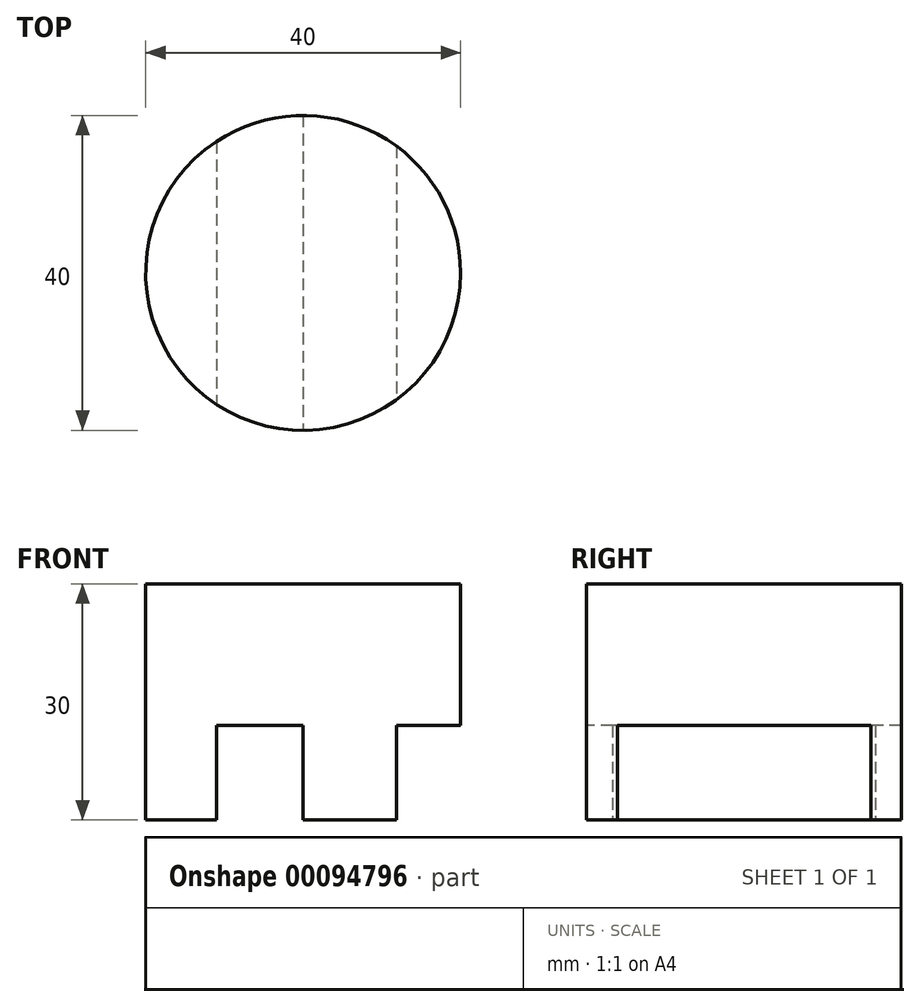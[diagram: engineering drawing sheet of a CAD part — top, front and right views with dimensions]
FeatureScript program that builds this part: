
annotation { "Feature Type Name" : "Feature", "Feature Type Description" : "" }
export const myFeature = defineFeature(function(context is Context, id is Id, definition is map)
    precondition{}
    {
        {
            var Q0;
            Q0=qCreatedBy(makeId("Top.planeOp"),FACE);
            var sketch = newSketch(context, id + "F0", { "sketchPlane" : qUnion([Q0])});
            skCircle(sketch, "E0", {"center": v(0, 0) * mm, "radius": 20 * mm});
            skSolve(sketch);
        }
        {
            var Q0;
            Q0=makeQuery(id+"F0.imprint","IMPRINT",FACE,{"disambiguationData":[TD([[makeQuery(id+"F0.imprint","IMPRINT",EDGE,{"derivedFrom":sQuery(id+"F0.wireOp",EDGE,"E0")}),1.0]])]});
            extrude(context, id + "F1", {"entities" : qUnion([Q0]), "depth" : 30 * mm});
        }
        {
            var Q0;
            Q0=qCreatedBy(makeId("Top.planeOp"),FACE);
            var sketch = newSketch(context, id + "F2", { "sketchPlane" : qUnion([Q0])});
            skLineSegment(sketch, "E1.bottom", {"start": v(0, 41.25) * mm, "end": v(-11.02, 41.25) * mm});
            skLineSegment(sketch, "E1.top", {"start": v(0, -40.16) * mm, "end": v(-11.02, -40.16) * mm});
            skLineSegment(sketch, "E1.left", {"start": v(0, 41.25) * mm, "end": v(0, -40.16) * mm});
            skLineSegment(sketch, "E1.right", {"start": v(-11.02, 41.25) * mm, "end": v(-11.02, -40.16) * mm});
            skSolve(sketch);
        }
        {
            var Q0;
            Q0 = qSketchRegion(id + "F2", true);
            extrude(context, id + "F3", {"entities" : qUnion([Q0]), "operationType" : NewBodyOperationType.REMOVE, "oppositeDirection" : true, "depth" : 12 * mm, "hasSecondDirection" : true, "secondDirectionOppositeDirection" : false, "secondDirectionDepth" : 12 * mm});
        }
        {
            var Q0;
            Q0=qCreatedBy(makeId("Top.planeOp"),FACE);
            var sketch = newSketch(context, id + "F4", { "sketchPlane" : qUnion([Q0])});
            skLineSegment(sketch, "E2.bottom", {"start": v(11.87, 20.4) * mm, "end": v(23.46, 20.4) * mm});
            skLineSegment(sketch, "E2.top", {"start": v(11.87, -28.38) * mm, "end": v(23.46, -28.38) * mm});
            skLineSegment(sketch, "E2.left", {"start": v(11.87, 20.4) * mm, "end": v(11.87, -28.38) * mm});
            skLineSegment(sketch, "E2.right", {"start": v(23.46, 20.4) * mm, "end": v(23.46, -28.38) * mm});
            skSolve(sketch);
        }
        {
            var Q0;
            Q0 = qSketchRegion(id + "F4", true);
            extrude(context, id + "F5", {"entities" : qUnion([Q0]), "operationType" : NewBodyOperationType.REMOVE, "depth" : 12 * mm});
        }
    });
